# Revit family: Hager-VOLTA-Surface_mounted-IP30-With_Cover-With_DIN-Hosted-PL-en
name_source: partatom
category: Electrical Equipment
units: mm (PartAtom-declared; Revit-internal decimal feet)

## family parameters
Cut with Voids When Loaded = No
Host = Face
Maintain Annotation Orientation = Yes
Panel Configuration = Two Columns, Circuits Across
Part Type = Panelboard
Room Calculation Point = No
Round Connector Dimension = Use Diameter
Shared = No

## types (6) — shared parameters
BC_MODEL_ID = 1547258
BC_OBJECT_ID = 513501
BC_OBJECT_VERSION = #5
Code hager = ADD-EC000214_EU
EF000003 - Mounting method = Surface mounted
EF000008 - Width = 305 mm  [stored 1.00066 ft]
EF000024 - UV resistant = No
EF000049 - Depth = 96 mm  [stored 0.314961 ft]
EF000116 - RAL-number = 9010
EF001062 - EMC-version = No
EF001088 - Extension possible = Yes
EF001134 - DIN-rail = Yes
EF002950 - Width in number of modular spacings = 12
EF005474 - Degree of protection (IP) = IP30
EF006244 - Transparent cover/door = No
EF006306 - With lock = No
EF009212 - Cover model = With notch
ETIM class code = EC000214
ETIM class name = Small distribution board
HG000002-With door or cover = Yes
HG000003-Range = VOLTA
HG000005-Thickness = 2 mm  [stored 0.00656168 ft]
HG000006-Flush mounted = No
HG000009-Double swing door = No
HG000010-Asymmetric doors = No
HG000012-Door swing angle = 90.00°
HG000013-Door on the left = No
HG000014-Door on the right = Yes
HG000015-Clearance visibility = Yes
HG000016-Door 3D visibility = Yes
HG000017-Distance between poles = 18 mm  [stored 0.0590551 ft]
HG000060-RAL-number = 9010
HG000099-Onfly Template ID = 507532
HGEF002950-Width in number of modular spacings = 12
Manufacturer = Hager
Name = VOLTA-Surface_mounted-IP30-With_Cover-With_DIN-PL
Name BIM&CO = Electricity
Name hager = ADD_Enclosures_EC000214
Uniformat = Low Tension Service & Dist.
Uniformat code = D501001
zero-valued in all types: Default Elevation, EF000218 - Built-in depth, EF000846 - Built-in width, EF001131 - Inner depth, HG000007-Number of empty columns

## per-type parameters (varying)
| type | BC_VARIANT_ID | EF000007 - Colour | EF000040 - Height | EF000118 - With mounting plate | EF000266 - Number of rows | EF000332 - Built-in height | EF004462 - Type of closure | EF015776 - Earthing terminal block | EF015777 - Neutral terminal block | EF015941 - Signal passing door | HG000001-Number of columns | HG000004-Manufacturer reference | HG000008-Number of empty rows | HG000011-Empty rows from bottom | HGEF000266-Number of rows |
| VOLTA-Surface_mounted_W305_H640_D96_12_Modular_Spacing-VA48NWB | 1174331 |  | 640 mm  [stored 2.09974 ft] | No | 0 | 0 mm  [stored 0 ft] |  | No | No | No | 0 | VA48NWB | 0 | No | 0 |
| VOLTA-Surface_mounted_W305_H765_D96_12_Modular_Spacing-VA602NWH | 1174332 | White | 765 mm  [stored 2.50984 ft] | Yes | 5 | 765 mm  [stored 2.50984 ft] | Other | Yes | Yes | No | 1 | VA602NWH | 3 | Yes | 5 |
| VOLTA-Surface_mounted_W305_H765_D96_12_Modular_Spacing-VA602WWH | 1174333 | White | 765 mm  [stored 2.50984 ft] | Yes | 5 | 765 mm  [stored 2.50984 ft] | Other | Yes | Yes | Yes | 1 | VA602WWH | 3 | Yes | 5 |
| VOLTA-Surface_mounted_W305_H765_D96_12_Modular_Spacing-VA603NWH | 1174334 | White | 765 mm  [stored 2.50984 ft] | Yes | 5 | 765 mm  [stored 2.50984 ft] | Other | Yes | Yes | No | 1 | VA603NWH | 2 | Yes | 5 |
| VOLTA-Surface_mounted_W305_H765_D96_12_Modular_Spacing-VA603WWH | 1174335 | White | 765 mm  [stored 2.50984 ft] | Yes | 5 | 765 mm  [stored 2.50984 ft] | Other | Yes | Yes | Yes | 1 | VA603WWH | 2 | Yes | 5 |
| VOLTA-Surface_mounted_W305_H765_D96_12_Modular_Spacing-VA60CN | 1174336 | White | 765 mm  [stored 2.50984 ft] | No | 5 | 0 mm  [stored 0 ft] |  | Yes | Yes | No | 1 | VA60CN | 0 | No | 5 |

note: column(s) folded — value = type name in every type: Reference

note: [stored X ft] marks values corroborated as IEEE doubles in the binary element streams (Revit-internal decimal feet)

## geometry (parser evidence)
native form markers: Sweep x14
no freeform markers — native parametric forms only
